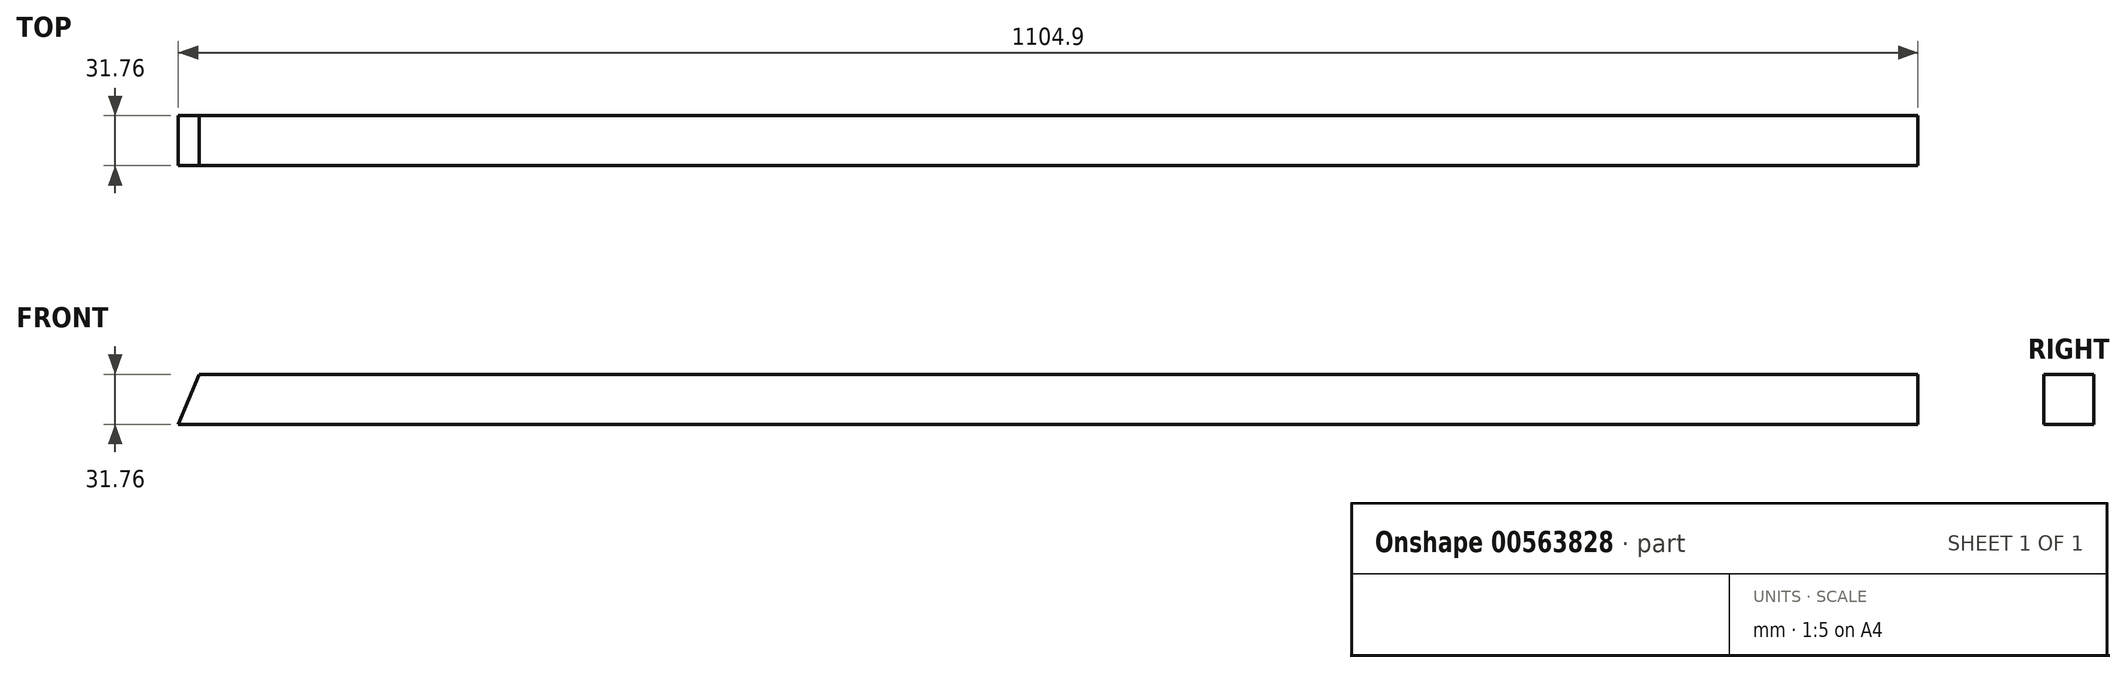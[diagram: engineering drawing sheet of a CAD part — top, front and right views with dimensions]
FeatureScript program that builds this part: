
annotation { "Feature Type Name" : "Feature", "Feature Type Description" : "" }
export const myFeature = defineFeature(function(context is Context, id is Id, definition is map)
    precondition{}
    {
        {
            var Q0;
            Q0=qCreatedBy(makeId("Front.planeOp"),FACE);
            var sketch = newSketch(context, id + "F0", { "sketchPlane" : qUnion([Q0])});
            skLineSegment(sketch, "E0.bottom", {"start": v(-552.45, 15.87) * mm, "end": v(552.45, 15.87) * mm});
            skLineSegment(sketch, "E0.top", {"start": v(-552.45, -15.88) * mm, "end": v(552.45, -15.88) * mm});
            skLineSegment(sketch, "E0.left", {"start": v(-552.45, 15.87) * mm, "end": v(-552.45, -15.88) * mm});
            skLineSegment(sketch, "E0.right", {"start": v(552.45, 15.87) * mm, "end": v(552.45, -15.88) * mm});
            skPoint(sketch, "E0.middle", {"position": v(0, 0) * mm});
            skLineSegment(sketch, "E1", {"start": v(-552.45, -15.87) * mm, "end": v(-539.3, 15.88) * mm});
            skSolve(sketch);
        }
        {
            var Q0;
            Q0=makeQuery(id+"F0.imprint","IMPRINT",FACE,{"disambiguationData":[TD([[makeQuery(id+"F0.imprint","IMPRINT",EDGE,{"derivedFrom":sQuery(id+"F0.wireOp",EDGE,"E0.top")}),1.0]])]});
            extrude(context, id + "F1", {"entities" : qUnion([Q0]), "endBound" : BoundingType.SYMMETRIC, "depth" : 31.75 * mm, "offsetDistance" : 25.4 * mm});
        }
    });
